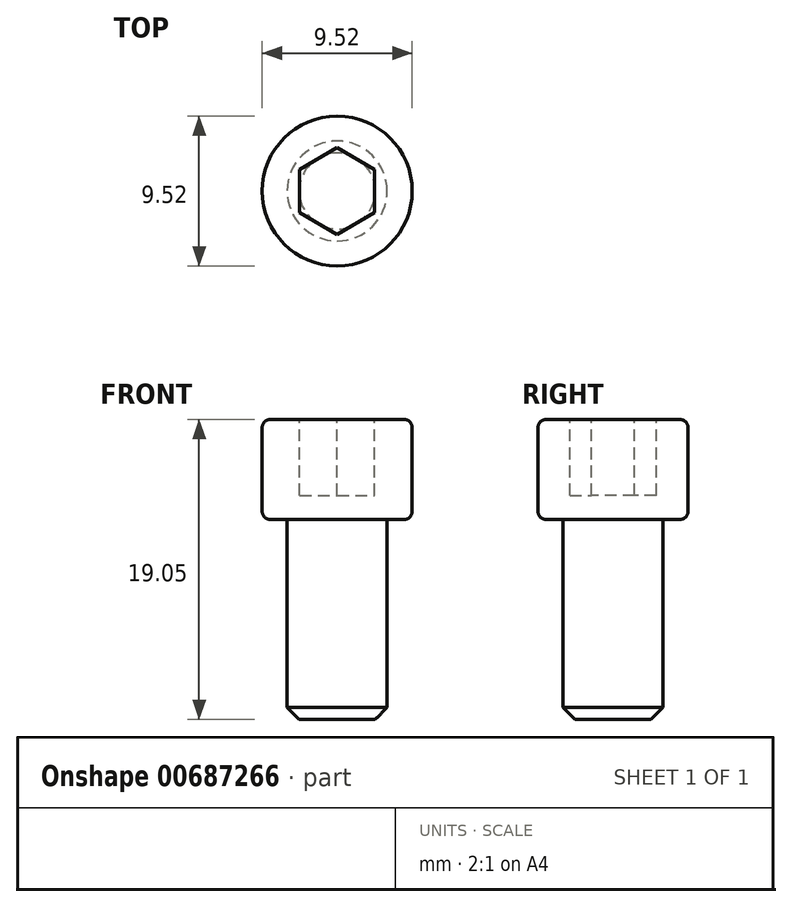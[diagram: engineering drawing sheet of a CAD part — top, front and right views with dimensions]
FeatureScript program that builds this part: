
annotation { "Feature Type Name" : "Feature", "Feature Type Description" : "" }
export const myFeature = defineFeature(function(context is Context, id is Id, definition is map)
    precondition{}
    {
        {
            var Q0;
            Q0=qCreatedBy(makeId("Top.planeOp"),FACE);
            var sketch = newSketch(context, id + "F0", { "sketchPlane" : qUnion([Q0])});
            skCircle(sketch, "E0", {"center": v(0, 0) * mm, "radius": 3.18 * mm});
            skSolve(sketch);
        }
        {
            var Q0;
            Q0=makeQuery(id+"F0.imprint","IMPRINT",FACE,{"disambiguationData":[TD([[makeQuery(id+"F0.imprint","IMPRINT",EDGE,{"derivedFrom":sQuery(id+"F0.wireOp",EDGE,"E0")}),1.0]])]});
            extrude(context, id + "F1", {"entities" : qUnion([Q0]), "oppositeDirection" : true, "depth" : 12.7 * mm});
        }
        {
            var Q0;
            Q0=qCreatedBy(makeId("Top.planeOp"),FACE);
            var sketch = newSketch(context, id + "F2", { "sketchPlane" : qUnion([Q0])});
            skCircle(sketch, "E1", {"center": v(0, 0) * mm, "radius": 4.76 * mm});
            skSolve(sketch);
        }
        {
            var Q0;
            Q0=makeQuery(id+"F2.imprint","IMPRINT",FACE,{"disambiguationData":[TD([[makeQuery(id+"F2.imprint","IMPRINT",EDGE,{"derivedFrom":sQuery(id+"F2.wireOp",EDGE,"E1")}),1.0]])]});
            extrude(context, id + "F3", {"entities" : qUnion([Q0]), "operationType" : NewBodyOperationType.ADD, "depth" : 6.35 * mm});
        }
        {
            var Q0;
            Q0=makeQuery(id+"F3.opExtrude","CAP_FACE",FACE,{"disambiguationData":[OSD([sQuery(id+"F2.wireOp",EDGE,"E1")])],"isStart":false});
            var sketch = newSketch(context, id + "F4", { "sketchPlane" : qUnion([Q0])});
            skCircle(sketch, "E2.cCircle", {"center": v(0, 0) * mm, "radius": 2.38 * mm, "construction": true});
            skLineSegment(sketch, "E2.0", {"start": v(2.38, 1.37) * mm, "end": v(2.38, -1.37) * mm});
            skLineSegment(sketch, "E2.1", {"start": v(2.38, -1.37) * mm, "end": v(0, -2.75) * mm});
            skLineSegment(sketch, "E2.2", {"start": v(0, -2.75) * mm, "end": v(-2.38, -1.37) * mm});
            skLineSegment(sketch, "E2.3", {"start": v(-2.38, -1.37) * mm, "end": v(-2.38, 1.37) * mm});
            skLineSegment(sketch, "E2.4", {"start": v(-2.38, 1.37) * mm, "end": v(0, 2.75) * mm});
            skLineSegment(sketch, "E2.5", {"start": v(0, 2.75) * mm, "end": v(2.38, 1.37) * mm});
            skPoint(sketch, "E2.0.midPoint", {"position": v(2.38, 0) * mm});
            skSolve(sketch);
        }
        {
            var Q0;
            Q0=makeQuery(id+"F4.imprint","IMPRINT",FACE,{"disambiguationData":[TD([[makeQuery(id+"F4.imprint","IMPRINT",EDGE,{"derivedFrom":sQuery(id+"F4.wireOp",EDGE,"E2.0")}),-1.0]])]});
            extrude(context, id + "F5", {"entities" : qUnion([Q0]), "operationType" : NewBodyOperationType.REMOVE, "oppositeDirection" : true, "depth" : 4.83 * mm});
        }
        {
            var Q0;
            Q0=makeQuery(id+"F1.opExtrude","CAP_EDGE",EDGE,{"disambiguationData":[OSD([sQuery(id+"F0.wireOp",EDGE,"E0")])],"isStart":false});
            chamfer(context, id + "F6", {"entities" : qUnion([Q0]), "chamferType" : ChamferType.OFFSET_ANGLE, "width" : 0.76 * mm, "oppositeDirection" : false, "angle" : 45 * degree, "tangentPropagation" : true});
        }
        {
            var Q0;
            Q0=qCreatedBy(makeId("Top.planeOp"),FACE);
            cPlane(context, id + "F7", {"entities" : qUnion([Q0]), "cplaneType" : CPlaneType.OFFSET, "offset" : ((1 / 20) * 2) * mm, "oppositeDirection" : true, "width" : 152.4 * mm, "height" : 152.4 * mm});
        }
        {
            var Q0;
            Q0=qCreatedBy(id+"F7.planeOp",FACE);
            var sketch = newSketch(context, id + "F8", { "sketchPlane" : qUnion([Q0])});
            skCircle(sketch, "E3", {"center": v(0, 0) * mm, "radius": 2.38 * mm});
            skSolve(sketch);
        }
        {
            var Q0;
            Q0=sQuery(id+"F8.wireOp",EDGE,"E3");
            var Q1;
            Q1=makeQuery(id+"F6.opChamfer","BLEND_FACE",FACE,{"disambiguationData":[OSD([sQuery(id+"F0.wireOp",EDGE,"E0")])]});
            extrude(context, id + "F9", {"bodyType" : ExtendedToolBodyType.SURFACE, "surfaceEntities" : qUnion([Q0]), "endBound" : BoundingType.UP_TO_SURFACE, "oppositeDirection" : true, "endBoundEntityFace" : qUnion([Q1]), "depth" : 25.4 * mm});
        }
        {
            var Q0;
            Q0=makeQuery(id+"F3.opExtrude","CAP_EDGE",EDGE,{"disambiguationData":[OSD([sQuery(id+"F2.wireOp",EDGE,"E1")])],"isStart":false});
            var Q1;
            Q1=makeQuery(id+"F3.opExtrude","CAP_EDGE",EDGE,{"disambiguationData":[OSD([sQuery(id+"F2.wireOp",EDGE,"E1")])],"isStart":true});
            fillet(context, id + "F10", {"entities" : qUnion([Q0, Q1]), "radius" : 0.5 * mm, "tangentPropagation" : true, "allowEdgeOverflow" : false});
        }
    });
